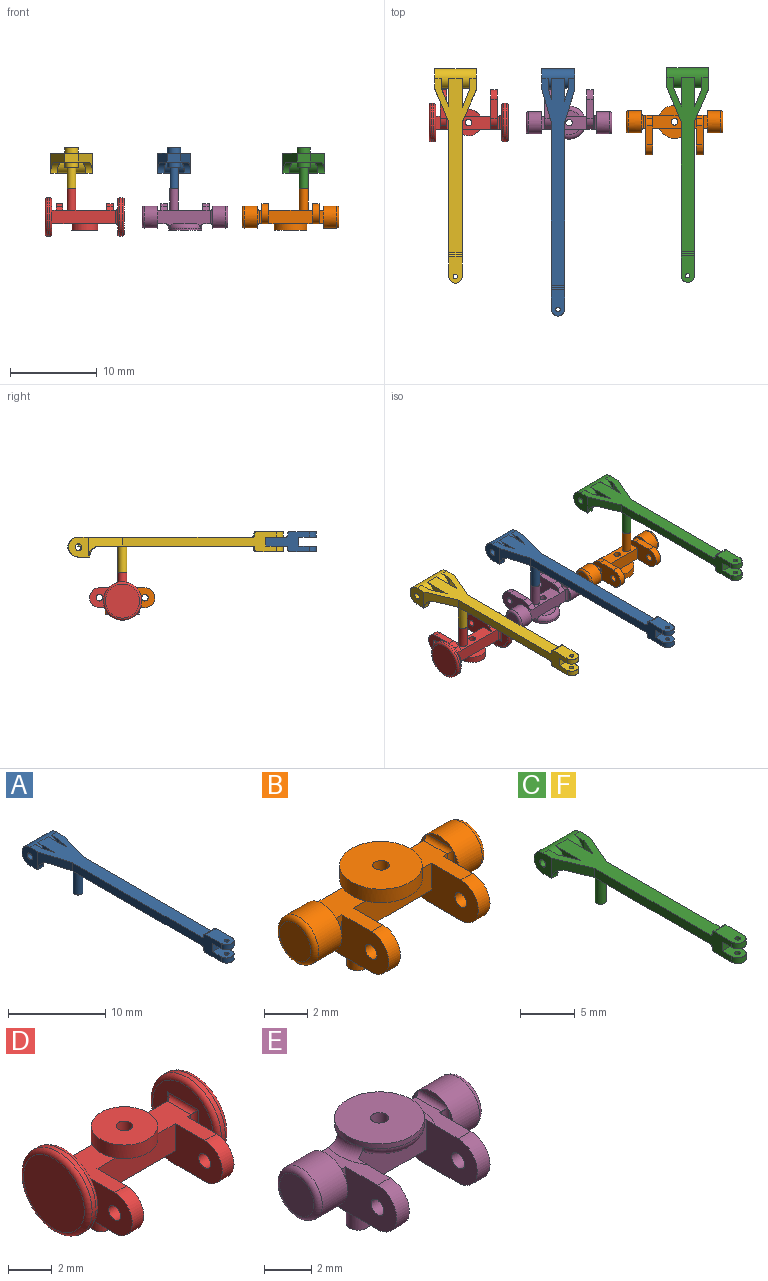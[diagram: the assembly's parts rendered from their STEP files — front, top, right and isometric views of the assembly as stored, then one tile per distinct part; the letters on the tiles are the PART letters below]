
ASSEMBLY  parts=6 mates=9
PART A: 39 faces, bbox 3.8x28.6x4.7 mm
  f0: plane 23.88x3.84mm, normal (0,0,1), area 42.2mm2, adj f1,f2,f4,f6,f7,f9,f10,f11
  f1: cylinder r=1.14mm len=3.84mm, axis (1,0,0), area 19.2mm2, adj f0,f2,f3,f4,f5,f6,f7,f8
  f2: plane 1.14x1.14mm, normal (1,0,0), area 0.3mm2, adj f0,f1,f12
  f3: plane 1.14x1.14mm, normal (1,0,0), area 0.3mm2, adj f1,f5,f12
  f4: plane 2.29x2.29mm, normal (-1,0,0), area 4.2mm2, adj f0,f1,f5,f13,f19
  f5: plane 1.14x0.76mm, normal (0,0,-1), area 0.9mm2, adj f1,f3,f4,f35
  f6: plane 2.29x1.29mm, normal (-1,0,0), area 0.9mm2, adj f0,f1,f8,f9
  f7: plane 2.43x2.29mm, normal (1,0,0), area 4.5mm2, adj f0,f1,f8,f17,f19
  f8: plane 1.29x0.76mm, normal (0,0,-1), area 1mm2, adj f1,f6,f7,f36
  f9: plane 2.29x1.32mm, normal (-0.96,0.29,0), area 1.8mm2, adj f0,f6,f10,f18,f36
  f10: plane 2.61x1.25mm, normal (1,0,0), area 1.8mm2, adj f0,f1,f9,f18,f34
  f11: plane 2.46x1.25mm, normal (-1,0,0), area 1.6mm2, adj f0,f1,f12,f18,f34
  f12: plane 2.29x1.31mm, normal (0.96,0.28,0), area 1.7mm2, adj f0,f2,f3,f11,f18,f35
  f13: plane 3.94x2.29mm, normal (-0.96,-0.28,0), area 4.5mm2, adj f0,f4,f14,f18,f35
  f14: plane 21.59x2.29mm, normal (-1,0,0), area 23.9mm2, adj f0,f13,f15,f18,f20,f21,f22,f24
  f15: plane 1.52x1.02mm, normal (0,-1,0), area 1.5mm2, adj f14,f16,f20,f29
  f16: plane 21.59x2.29mm, normal (1,0,0), area 23.9mm2, adj f0,f15,f17,f18,f20,f21,f22,f24
  f17: plane 3.79x2.29mm, normal (0.96,-0.29,0), area 4.4mm2, adj f0,f7,f16,f18,f36
  f18: plane 22.48x3.08mm, normal (0,0,-1), area 35.5mm2, adj f9,f10,f11,f12,f13,f14,f16,f17
  f19: cylinder r=0.38mm len=3.84mm, axis (1,0,0), area 9.2mm2, adj f4,f7
  f20: plane 2.03x1.52mm, normal (0,0,-1), area 2.6mm2, adj f14,f15,f16,f22,f23
  f21: plane 1.52x0.13mm, normal (0,1,0), area 0.2mm2, adj f14,f16,f32,f33
  f22: cylinder r=0.76mm len=1.52mm, axis (0,0,-1), area 1.5mm2, adj f14,f16,f20,f24
  f23: cylinder r=0.25mm len=0.64mm, axis (0,0,-1), area 1mm2, adj f20,f24
  f24: plane 3.05x1.52mm, normal (0,0,1), area 4.2mm2, adj f14,f16,f22,f23,f33
  f25: plane 1.52x0.13mm, normal (0,1,0), area 0.2mm2, adj f14,f16,f30,f31
  f26: cylinder r=0.76mm len=1.52mm, axis (0,0,1), area 1.5mm2, adj f14,f16,f28,f29
  f27: cylinder r=0.25mm len=0.64mm, axis (0,0,1), area 1mm2, adj f28,f29
  f28: plane 3.05x1.52mm, normal (0,0,-1), area 4.2mm2, adj f14,f16,f26,f27,f31
  f29: plane 2.03x1.52mm, normal (0,0,1), area 2.6mm2, adj f14,f15,f16,f26,f27
  f30: cylinder r=0.25mm len=1.52mm, axis (-1,0,0), area 0.6mm2, adj f14,f16,f18,f25
  f31: cylinder r=0.25mm len=1.52mm, axis (-1,0,0), area 0.6mm2, adj f14,f16,f25,f28
  f32: cylinder r=0.25mm len=1.52mm, axis (-1,0,0), area 0.6mm2, adj f0,f14,f16,f21
  f33: cylinder r=0.25mm len=1.52mm, axis (1,0,0), area 0.6mm2, adj f14,f16,f21,f24
  f34: cylinder r=0.25mm len=1.52mm, axis (1,0,0), area 0.6mm2, adj f1,f10,f11,f18
  f35: cylinder r=1.27mm len=1.27mm, axis (-1,0,0), area 1.5mm2, adj f5,f12,f13,f18
  f36: cylinder r=1.27mm len=1.27mm, axis (-1,0,0), area 1.5mm2, adj f8,f9,f17,f18
  f37: cylinder r=0.51mm len=3.05mm, axis (0,0,1), area 9.7mm2, adj f18,f38
  f38: plane 1.02x1.02mm, normal (0,0,-1), area 0.8mm2, adj f37
PART B: 45 faces, bbox 11.2x5.7x4.8 mm
  f0: plane 1.52x0.25mm, normal (-1,0,0), area 0.3mm2, adj f32,f38
  f1: plane 1.52x0.25mm, normal (-1,0,0), area 0.3mm2, adj f32,f35
  f2: plane 1.52x0.25mm, normal (-1,0,0), area 0.3mm2, adj f32,f37
  f3: plane 1.52x0.25mm, normal (0,0,-1), area 0.4mm2, adj f8,f9,f20,f36
  f4: plane 5.08x1.52mm, normal (0,0,-1), area 6.5mm2, adj f5,f8,f17,f19,f30,f43
  f5: plane 5.08x1.52mm, normal (0,-1,0), area 7.7mm2, adj f4,f7,f11,f12,f17,f19
  f6: plane 1.52x0.51mm, normal (0,-1,0), area 0.8mm2, adj f7,f10,f16,f41
  f7: plane 3.43x2.06mm, normal (0,0,1), area 4.4mm2, adj f5,f6,f8,f13,f16,f17,f26,f41
  f8: plane 7.37x1.52mm, normal (0,1,0), area 11.2mm2, adj f3,f4,f7,f10,f11,f15,f22,f23
  f9: plane 1.52x0.25mm, normal (0,-1,0), area 0.4mm2, adj f3,f11,f20,f38
  f10: plane 1.52x0.51mm, normal (0,0,-1), area 0.8mm2, adj f6,f8,f16,f41
  f11: plane 3.43x1.81mm, normal (0,0,1), area 4mm2, adj f5,f8,f9,f13,f19,f20,f27,f37
  f12: plane 3.49x1.14mm, normal (0,0,-1), area 2.9mm2, adj f5,f13
  f13: cylinder r=1.91mm len=3.81mm, axis (0,0,-1), area 9.1mm2, adj f7,f11,f12,f14,f15
  f14: plane 3.81x3.81mm, normal (0,0,1), area 10.9mm2, adj f13,f30
  f15: plane 3.49x1.14mm, normal (0,0,-1), area 2.9mm2, adj f8,f13
  f16: plane 4.57x2.29mm, normal (-1,0,0), area 6.8mm2, adj f6,f7,f10,f18,f23,f24,f26,f29
  f17: plane 4.57x2.29mm, normal (1,0,0), area 6.8mm2, adj f4,f5,f7,f18,f23,f24,f26,f29
  f18: plane 2.19x0.76mm, normal (0,0,-1), area 1.7mm2, adj f16,f17,f24,f26
  f19: plane 4.57x2.29mm, normal (-1,0,0), area 6.8mm2, adj f4,f5,f11,f21,f22,f25,f27,f28
  f20: plane 4.57x2.29mm, normal (1,0,0), area 6.8mm2, adj f3,f9,f11,f21,f22,f25,f27,f28
  f21: plane 2.19x0.76mm, normal (0,0,-1), area 1.7mm2, adj f19,f20,f25,f27
  f22: plane 0.76x0.43mm, normal (0,0.71,-0.71), area 0.5mm2, adj f8,f19,f20,f25
  f23: plane 0.76x0.43mm, normal (0,0.71,-0.71), area 0.5mm2, adj f8,f16,f17,f24
  f24: cylinder r=1.14mm len=0.81mm, axis (-1,0,0), area 0.7mm2, adj f16,f17,f18,f23
  f25: cylinder r=1.14mm len=0.81mm, axis (-1,0,0), area 0.7mm2, adj f19,f20,f21,f22
  f26: cylinder r=1.14mm len=2.29mm, axis (-1,0,0), area 2.7mm2, adj f7,f16,f17,f18
  f27: cylinder r=1.14mm len=2.29mm, axis (-1,0,0), area 2.7mm2, adj f11,f19,f20,f21
  f28: cylinder r=0.38mm len=0.76mm, axis (1,0,0), area 1.8mm2, adj f19,f20
  f29: cylinder r=0.38mm len=0.76mm, axis (1,0,0), area 1.8mm2, adj f16,f17
  f30: cylinder r=0.38mm len=2.29mm, axis (0,0,1), area 5.5mm2, adj f4,f14
  f31: plane 1.52x0.25mm, normal (-1,0,0), area 0.3mm2, adj f32,f36
  f32: cylinder r=1.27mm len=2.54mm, axis (-1,0,0), area 12.2mm2, adj f0,f1,f2,f31,f34,f35,f36,f37
  f33: plane 2.03x2.03mm, normal (1,0,0), area 3.2mm2, adj f34
  f34: torus R=1.02mm, axis (1,0,0), area 3mm2, adj f32,f33
  f35: cylinder r=0.25mm len=1.8mm, axis (0,0,-1), area 0.7mm2, adj f1,f8,f32,f36,f37
  f36: cylinder r=0.25mm len=1.8mm, axis (0,1,0), area 0.7mm2, adj f3,f31,f32,f35,f38
  f37: cylinder r=0.25mm len=1.8mm, axis (0,-1,0), area 0.7mm2, adj f2,f11,f32,f35,f38
  f38: cylinder r=0.25mm len=1.8mm, axis (0,0,1), area 0.7mm2, adj f0,f9,f32,f36,f37
  f39: cylinder r=1.27mm len=2.54mm, axis (1,0,0), area 12.2mm2, adj f41,f42
  f40: plane 2.03x2.03mm, normal (-1,0,0), area 3.2mm2, adj f42
  f41: plane 2.54x2.54mm, normal (1,0,0), area 2.7mm2, adj f6,f7,f8,f10,f39
  f42: torus R=1.02mm, axis (-1,0,0), area 3mm2, adj f39,f40
  f43: cylinder r=0.51mm len=2.54mm, axis (0,0,1), area 8.1mm2, adj f4,f44
  f44: plane 1.02x1.02mm, normal (0,0,-1), area 0.8mm2, adj f43
PART C: 43 faces, bbox 4.8x24.8x4.7 mm
  f0: plane 20.07x4.83mm, normal (0,0,1), area 37mm2, adj f1,f3,f5,f7,f8,f14,f15,f16
  f1: cylinder r=1.14mm len=4.83mm, axis (1,0,0), area 26.3mm2, adj f0,f3,f4,f5,f6,f7,f8,f9
  f2: cylinder r=0.38mm len=4.83mm, axis (1,0,0), area 10.8mm2, adj f5,f8,f10,f11,f12,f13
  f3: plane 1.14x1.14mm, normal (1,0,0), area 0.3mm2, adj f0,f1,f17
  f4: plane 1.14x1.14mm, normal (1,0,0), area 0.3mm2, adj f1,f6,f17
  f5: plane 2.29x2.29mm, normal (-1,0,0), area 4.2mm2, adj f0,f1,f2,f6,f18
  f6: plane 1.14x0.76mm, normal (0,0,-1), area 0.9mm2, adj f1,f4,f5,f39
  f7: plane 2.29x1.29mm, normal (-1,0,0), area 0.9mm2, adj f0,f1,f9,f14
  f8: plane 2.43x2.29mm, normal (1,0,0), area 4.5mm2, adj f0,f1,f2,f9,f22
  f9: plane 1.29x0.76mm, normal (0,0,-1), area 1mm2, adj f1,f7,f8,f40
  f10: plane 1.52x0.36mm, normal (0,0,-1), area 0.5mm2, adj f2,f11,f12,f13
  f11: plane 0.36x0.25mm, normal (-1,0,0), area 0.1mm2, adj f2,f10,f12
  f12: plane 1.52x0.25mm, normal (0,1,0), area 0.4mm2, adj f2,f10,f11,f13
  f13: plane 0.36x0.25mm, normal (1,0,0), area 0.1mm2, adj f2,f10,f12
  f14: plane 2.29x2.04mm, normal (-0.92,0.4,0), area 2.6mm2, adj f0,f7,f15,f23,f40
  f15: plane 3.33x1.25mm, normal (1,0,0), area 2.5mm2, adj f0,f1,f14,f23,f38
  f16: plane 3.26x1.25mm, normal (-1,0,0), area 2.4mm2, adj f0,f1,f17,f23,f38
  f17: plane 2.29x2.12mm, normal (0.92,0.39,0), area 2.7mm2, adj f0,f3,f4,f16,f23,f39
  f18: plane 3.94x2.29mm, normal (-0.92,-0.39,0), area 4.7mm2, adj f0,f5,f19,f23,f39
  f19: plane 17.78x2.29mm, normal (-1,0,0), area 20mm2, adj f0,f18,f20,f23,f24,f25,f26,f28
  f20: plane 1.52x1.02mm, normal (0,-1,0), area 1.5mm2, adj f19,f21,f24,f33
  f21: plane 17.78x2.29mm, normal (1,0,0), area 20mm2, adj f0,f20,f22,f23,f24,f25,f26,f28
  f22: plane 3.79x2.29mm, normal (0.92,-0.4,0), area 4.6mm2, adj f0,f8,f21,f23,f40
  f23: plane 18.67x3.74mm, normal (0,0,-1), area 30.2mm2, adj f14,f15,f16,f17,f18,f19,f21,f22
  f24: plane 2.03x1.52mm, normal (0,0,-1), area 2.6mm2, adj f19,f20,f21,f26,f27
  f25: plane 1.52x0.13mm, normal (0,1,0), area 0.2mm2, adj f19,f21,f36,f37
  f26: cylinder r=0.76mm len=1.52mm, axis (0,0,-1), area 1.5mm2, adj f19,f21,f24,f28
  f27: cylinder r=0.25mm len=0.64mm, axis (0,0,-1), area 1mm2, adj f24,f28
  f28: plane 3.05x1.52mm, normal (0,0,1), area 4.2mm2, adj f19,f21,f26,f27,f37
  f29: plane 1.52x0.13mm, normal (0,1,0), area 0.2mm2, adj f19,f21,f34,f35
  f30: cylinder r=0.76mm len=1.52mm, axis (0,0,1), area 1.5mm2, adj f19,f21,f32,f33
  f31: cylinder r=0.25mm len=0.64mm, axis (0,0,1), area 1mm2, adj f32,f33
  f32: plane 3.05x1.52mm, normal (0,0,-1), area 4.2mm2, adj f19,f21,f30,f31,f35
  f33: plane 2.03x1.52mm, normal (0,0,1), area 2.6mm2, adj f19,f20,f21,f30,f31
  f34: cylinder r=0.25mm len=1.52mm, axis (-1,0,0), area 0.6mm2, adj f19,f21,f23,f29
  f35: cylinder r=0.25mm len=1.52mm, axis (-1,0,0), area 0.6mm2, adj f19,f21,f29,f32
  f36: cylinder r=0.25mm len=1.52mm, axis (-1,0,0), area 0.6mm2, adj f0,f19,f21,f25
  f37: cylinder r=0.25mm len=1.52mm, axis (1,0,0), area 0.6mm2, adj f19,f21,f25,f28
  f38: cylinder r=0.25mm len=1.52mm, axis (1,0,0), area 0.6mm2, adj f1,f15,f16,f23
  f39: cylinder r=1.27mm len=1.29mm, axis (-1,0,0), area 1.5mm2, adj f6,f17,f18,f23
  f40: cylinder r=1.27mm len=1.31mm, axis (-1,0,0), area 1.5mm2, adj f9,f14,f22,f23
  f41: cylinder r=0.51mm len=3.05mm, axis (0,0,1), area 9.7mm2, adj f23,f42
  f42: plane 1.02x1.02mm, normal (0,0,-1), area 0.8mm2, adj f41
PART D: 44 faces, bbox 9.1x6.2x5.7 mm
  f0: plane 1.52x0.25mm, normal (0,0,-1), area 0.4mm2, adj f5,f6,f17,f34
  f1: plane 5.08x1.52mm, normal (0,0,-1), area 6.5mm2, adj f2,f5,f14,f16,f27,f42
  f2: plane 5.08x1.52mm, normal (0,-1,0), area 7.7mm2, adj f1,f4,f8,f9,f14,f16
  f3: plane 1.52x0.51mm, normal (0,-1,0), area 0.8mm2, adj f4,f7,f13,f39
  f4: plane 3.43x2.49mm, normal (0,0,1), area 5mm2, adj f2,f3,f5,f10,f13,f14,f23,f39
  f5: plane 7.37x1.52mm, normal (0,1,0), area 11.2mm2, adj f0,f1,f4,f7,f8,f12,f19,f20
  f6: plane 1.52x0.25mm, normal (0,-1,0), area 0.4mm2, adj f0,f8,f17,f36
  f7: plane 1.52x0.51mm, normal (0,0,-1), area 0.8mm2, adj f3,f5,f13,f39
  f8: plane 3.43x2.24mm, normal (0,0,1), area 4.6mm2, adj f2,f5,f6,f10,f16,f17,f24,f35
  f9: plane 2.64x0.76mm, normal (0,0,-1), area 1.4mm2, adj f2,f10
  f10: cylinder r=1.52mm len=3.05mm, axis (0,0,-1), area 7.3mm2, adj f4,f8,f9,f11,f12
  f11: plane 3.05x3.05mm, normal (0,0,1), area 6.8mm2, adj f10,f27
  f12: plane 2.64x0.76mm, normal (0,0,-1), area 1.4mm2, adj f5,f10
  f13: plane 4.57x2.29mm, normal (-1,0,0), area 6.8mm2, adj f3,f4,f7,f15,f20,f21,f23,f26
  f14: plane 4.57x2.29mm, normal (1,0,0), area 6.8mm2, adj f1,f2,f4,f15,f20,f21,f23,f26
  f15: plane 2.19x0.76mm, normal (0,0,-1), area 1.7mm2, adj f13,f14,f21,f23
  f16: plane 4.57x2.29mm, normal (-1,0,0), area 6.8mm2, adj f1,f2,f8,f18,f19,f22,f24,f25
  f17: plane 4.57x2.29mm, normal (1,0,0), area 6.8mm2, adj f0,f6,f8,f18,f19,f22,f24,f25
  f18: plane 2.19x0.76mm, normal (0,0,-1), area 1.7mm2, adj f16,f17,f22,f24
  f19: plane 0.76x0.43mm, normal (0,0.71,-0.71), area 0.5mm2, adj f5,f16,f17,f22
  f20: plane 0.76x0.43mm, normal (0,0.71,-0.71), area 0.5mm2, adj f5,f13,f14,f21
  f21: cylinder r=1.14mm len=0.81mm, axis (-1,0,0), area 0.7mm2, adj f13,f14,f15,f20
  f22: cylinder r=1.14mm len=0.81mm, axis (-1,0,0), area 0.7mm2, adj f16,f17,f18,f19
  f23: cylinder r=1.14mm len=2.29mm, axis (-1,0,0), area 2.7mm2, adj f4,f13,f14,f15
  f24: cylinder r=1.14mm len=2.29mm, axis (-1,0,0), area 2.7mm2, adj f8,f16,f17,f18
  f25: cylinder r=0.38mm len=0.76mm, axis (1,0,0), area 1.8mm2, adj f16,f17
  f26: cylinder r=0.38mm len=0.76mm, axis (1,0,0), area 1.8mm2, adj f13,f14
  f27: cylinder r=0.38mm len=2.29mm, axis (0,0,1), area 5.5mm2, adj f1,f11
  f28: plane 3.94x3.94mm, normal (-1,0,0), area 8mm2, adj f31,f33,f34,f35,f36
  f29: cylinder r=2.22mm len=4.45mm, axis (-1,0,0), area 3.5mm2, adj f31,f32
  f30: plane 3.94x3.94mm, normal (1,0,0), area 12.2mm2, adj f32
  f31: torus R=1.97mm, axis (1,0,0), area 5.3mm2, adj f28,f29
  f32: torus R=1.97mm, axis (1,0,0), area 5.3mm2, adj f29,f30
  f33: cylinder r=0.25mm len=2.03mm, axis (0,0,-1), area 0.7mm2, adj f5,f28,f34,f35
  f34: cylinder r=0.25mm len=2.03mm, axis (0,1,0), area 0.7mm2, adj f0,f28,f33,f36
  f35: cylinder r=0.25mm len=2.03mm, axis (0,-1,0), area 0.7mm2, adj f8,f28,f33,f36
  f36: cylinder r=0.25mm len=2.03mm, axis (0,0,1), area 0.7mm2, adj f6,f28,f34,f35
  f37: cylinder r=2.22mm len=4.45mm, axis (1,0,0), area 3.5mm2, adj f40,f41
  f38: plane 3.94x3.94mm, normal (-1,0,0), area 12.2mm2, adj f41
  f39: plane 3.94x3.94mm, normal (1,0,0), area 9.9mm2, adj f3,f4,f5,f7,f40
  f40: torus R=1.97mm, axis (-1,0,0), area 5.3mm2, adj f37,f39
  f41: torus R=1.97mm, axis (-1,0,0), area 5.3mm2, adj f37,f38
  f42: cylinder r=0.51mm len=2.54mm, axis (0,0,1), area 8.1mm2, adj f1,f43
  f43: plane 1.02x1.02mm, normal (0,0,-1), area 0.8mm2, adj f42
PART E: 49 faces, bbox 9.9x5.9x5 mm
  f0: plane 1.52x0.25mm, normal (-1,0,0), area 0.3mm2, adj f32,f38
  f1: plane 1.52x0.25mm, normal (-1,0,0), area 0.3mm2, adj f32,f35
  f2: plane 1.52x0.25mm, normal (-1,0,0), area 0.3mm2, adj f32,f37
  f3: plane 1.52x0.13mm, normal (0,0,-1), area 0.2mm2, adj f8,f9,f20,f36
  f4: plane 4.06x1.52mm, normal (0,0,-1), area 4.9mm2, adj f5,f8,f17,f19,f30,f43
  f5: plane 4.11x2.07mm, normal (0,-1,0), area 6.4mm2, adj f4,f12,f17,f19,f45,f47,f48
  f6: plane 1.52x0.38mm, normal (0,-1,0), area 0.6mm2, adj f7,f10,f16,f41
  f7: plane 3.43x1.14mm, normal (0,0,1), area 2.6mm2, adj f6,f8,f16,f17,f26,f41,f47
  f8: plane 6.1x2.03mm, normal (0,1,0), area 9.5mm2, adj f3,f4,f7,f10,f11,f15,f22,f23
  f9: plane 1.52x0.13mm, normal (0,-1,0), area 0.2mm2, adj f3,f11,f20,f38
  f10: plane 1.52x0.38mm, normal (0,0,-1), area 0.6mm2, adj f6,f8,f16,f41
  f11: plane 3.43x0.89mm, normal (0,0,1), area 2.2mm2, adj f8,f9,f19,f20,f27,f37,f48
  f12: plane 2.34x0.64mm, normal (0,0,-1), area 1mm2, adj f5,f45
  f13: cylinder r=1.91mm len=3.81mm, axis (0,0,-1), area 3mm2, adj f14,f45,f46,f47,f48
  f14: plane 3.81x3.81mm, normal (0,0,1), area 10.9mm2, adj f13,f30
  f15: plane 2.34x0.64mm, normal (0,0,-1), area 1mm2, adj f8,f46
  f16: plane 4.57x2.29mm, normal (-1,0,0), area 6.8mm2, adj f6,f7,f10,f18,f23,f24,f26,f29
  f17: plane 4.6x2.38mm, normal (1,0,0), area 6.8mm2, adj f4,f5,f7,f18,f23,f24,f26,f29
  f18: plane 2.19x0.76mm, normal (0,0,-1), area 1.7mm2, adj f16,f17,f24,f26
  f19: plane 4.6x2.38mm, normal (-1,0,0), area 6.8mm2, adj f4,f5,f11,f21,f22,f25,f27,f28
  f20: plane 4.57x2.29mm, normal (1,0,0), area 6.8mm2, adj f3,f9,f11,f21,f22,f25,f27,f28
  f21: plane 2.19x0.76mm, normal (0,0,-1), area 1.7mm2, adj f19,f20,f25,f27
  f22: plane 0.76x0.43mm, normal (0,0.71,-0.71), area 0.5mm2, adj f8,f19,f20,f25
  f23: plane 0.76x0.43mm, normal (0,0.71,-0.71), area 0.5mm2, adj f8,f16,f17,f24
  f24: cylinder r=1.14mm len=0.81mm, axis (-1,0,0), area 0.7mm2, adj f16,f17,f18,f23
  f25: cylinder r=1.14mm len=0.81mm, axis (-1,0,0), area 0.7mm2, adj f19,f20,f21,f22
  f26: cylinder r=1.14mm len=2.29mm, axis (-1,0,0), area 2.7mm2, adj f7,f16,f17,f18
  f27: cylinder r=1.14mm len=2.29mm, axis (-1,0,0), area 2.7mm2, adj f11,f19,f20,f21
  f28: cylinder r=0.38mm len=0.76mm, axis (1,0,0), area 1.8mm2, adj f19,f20
  f29: cylinder r=0.38mm len=0.76mm, axis (1,0,0), area 1.8mm2, adj f16,f17
  f30: cylinder r=0.38mm len=2.29mm, axis (0,0,1), area 5.5mm2, adj f4,f14
  f31: plane 1.52x0.25mm, normal (-1,0,0), area 0.3mm2, adj f32,f36
  f32: cylinder r=1.27mm len=2.54mm, axis (-1,0,0), area 12.2mm2, adj f0,f1,f2,f31,f34,f35,f36,f37
  f33: plane 2.03x2.03mm, normal (1,0,0), area 3.2mm2, adj f34
  f34: torus R=1.02mm, axis (1,0,0), area 3mm2, adj f32,f33
  f35: cylinder r=0.25mm len=1.8mm, axis (0,0,-1), area 0.7mm2, adj f1,f8,f32,f36,f37
  f36: cylinder r=0.25mm len=1.8mm, axis (0,1,0), area 0.7mm2, adj f3,f31,f32,f35,f38
  f37: cylinder r=0.25mm len=1.8mm, axis (0,-1,0), area 0.7mm2, adj f2,f11,f32,f35,f38
  f38: cylinder r=0.25mm len=1.8mm, axis (0,0,1), area 0.7mm2, adj f0,f9,f32,f36,f37
  f39: cylinder r=1.27mm len=2.54mm, axis (1,0,0), area 12.2mm2, adj f41,f42
  f40: plane 2.03x2.03mm, normal (-1,0,0), area 3.2mm2, adj f42
  f41: plane 2.54x2.54mm, normal (1,0,0), area 2.7mm2, adj f6,f7,f8,f10,f39
  f42: torus R=1.02mm, axis (-1,0,0), area 3mm2, adj f39,f40
  f43: cylinder r=0.51mm len=2.54mm, axis (0,0,1), area 8.1mm2, adj f4,f44
  f44: plane 1.02x1.02mm, normal (0,0,-1), area 0.8mm2, adj f43
  f45: torus R=1.4mm, axis (0,0,1), area 3.1mm2, adj f5,f12,f13
  f46: torus R=1.4mm, axis (0,0,1), area 3.1mm2, adj f8,f13,f15
  f47: torus R=2.41mm, axis (0,0,1), area 1.3mm2, adj f5,f7,f8,f13,f17
  f48: torus R=2.41mm, axis (0,0,1), area 1.3mm2, adj f5,f8,f11,f13,f19
PART F: same geometry as C
PLACE A t=(11.66,-10.55,10.25)mm
PLACE B rot(axis=(0,-1,0),180deg) t=(25.11,-16.68,4.4)mm
PLACE C t=(26.63,-10.46,10.25)mm
PLACE D rot(axis=(1,0,0),180deg) t=(1.35,-16.77,4.4)mm
PLACE E rot(axis=(1,0,0),180deg) t=(12.93,-16.77,4.4)mm
PLACE F t=(-0.18,-10.55,10.25)mm fixed
MATE cylindrical C.f41 <-> B.f43  axis (0,0,1) through (26.63,-16.68,9.99)mm
MATE planar D.f10 <-> E.f13  axis (0,0,-1) through (1.35,-16.77,3.64)mm
MATE parallel C.f19 <-> B.f20  axis (-1,0,0) through (25.87,-16.68,12.53)mm
MATE planar E.f13 <-> B.f13  axis (0,0,-1) through (12.93,-16.77,3.64)mm
MATE cylindrical D.f42 <-> F.f41  axis (0,0,-1) through (-0.18,-16.77,7.2)mm
MATE planar D.f42 <-> F.f41  axis (0,0,1) through (-0.18,-16.77,8.47)mm
MATE cylindrical E.f43 <-> A.f37  axis (0,0,-1) through (11.66,-16.77,7.2)mm
MATE planar C.f41 <-> B.f43  axis (0,0,-1) through (26.63,-16.68,8.47)mm
MATE planar E.f43 <-> A.f37  axis (0,0,1) through (11.66,-16.77,8.47)mm
